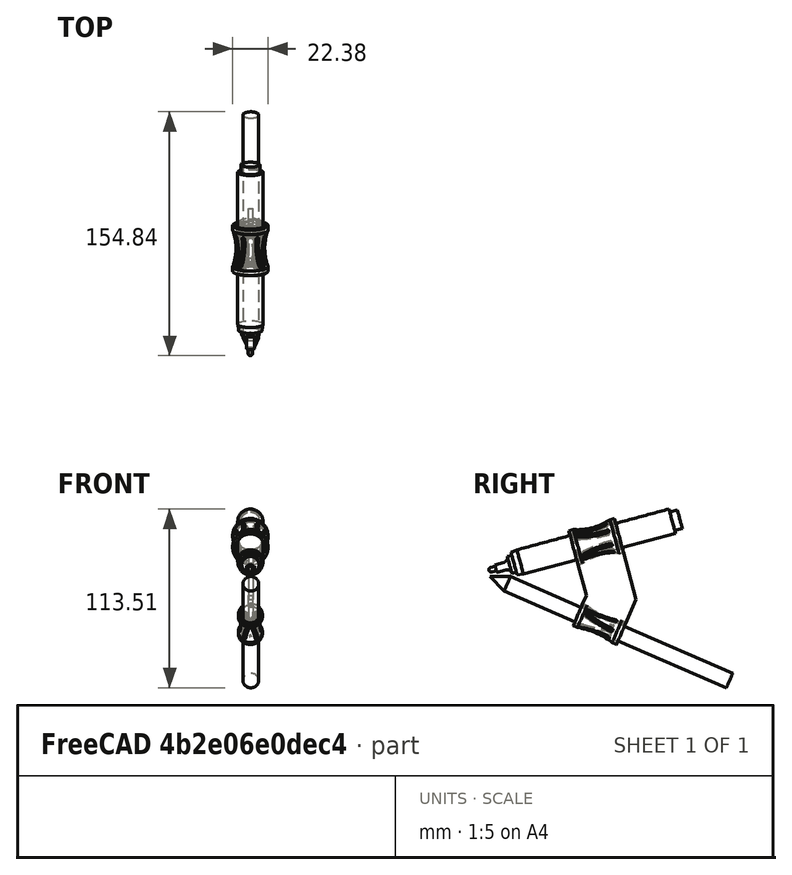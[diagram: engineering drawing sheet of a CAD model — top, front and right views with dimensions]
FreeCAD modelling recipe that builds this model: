
FCSTD DOCUMENT  (FreeCAD 1.0R39285 (Git))
Label: marker_holder_02
License: All rights reserved
LicenseURL: http://www.ohwr.org/attachments/2388/cern_ohl_v_1_2.txt
objects: PartDesign::SubShapeBinder×8, Sketcher::SketchObject×7, PartDesign::Plane×7, PartDesign::Body×5, PartDesign::Revolution×4, PartDesign::Line×3, PartDesign::Pocket×2, PartDesign::PolarPattern×2, PartDesign::Point×2, Mesh::Feature×1, PartDesign::Pad×1
note: 64 computed .brp shape members not serialized (recipe doc carries the construction recipe); baked Part::Feature solids carry a one-line shape summary decoded from their .brp

FEATURE [Mesh::Feature] Pencil_Hand_Pack
  Placement = pos=(0,0,0) rot=(-0.762035,0.457877,-0.457877;1.83927rad)
FEATURE [Sketcher::SketchObject] Sketch
  ArcFitTolerance = 1e-06
  AttachmentSupport = -> [YZ_Plane001]
  FullyConstrained = true
  MakeInternals = false
  MapMode = 5
  Placement = pos=(0,0,0) rot=(0.57735,0.57735,0.57735;2.0944rad)
  sketch-geometry (14):
    g0: LineSegment StartX=125.5 StartY=2e-16 StartZ=0 EndX=125.5 EndY=6 EndZ=0
    g1: LineSegment StartX=125.5 StartY=6 StartZ=0 EndX=120.5 EndY=6 EndZ=0
    g2: LineSegment StartX=120.5 StartY=6 StartZ=0 EndX=120.5 EndY=8 EndZ=0
    g3: LineSegment StartX=120.5 StartY=8 StartZ=0 EndX=28.5 EndY=8 EndZ=0
    g4: LineSegment StartX=28.5 StartY=8 StartZ=0 EndX=20.5 EndY=8 EndZ=0
    g5: LineSegment StartX=20.5 StartY=8 StartZ=0 EndX=16.5 EndY=7.5 EndZ=0
    g6: LineSegment StartX=16.5 StartY=7.5 StartZ=0 EndX=16.5 EndY=5.5 EndZ=0
    g7: LineSegment StartX=16.5 StartY=5.5 StartZ=0 EndX=13.5 EndY=5.5 EndZ=0
    g8: ArcOfCircle CenterX=10.5 CenterY=5.5 CenterZ=0 NormalX=0 NormalY=0 NormalZ=1 AngleXU=0 Radius=3 StartAngle=4.71239 EndAngle=6.28319
    g9: LineSegment StartX=10.5 StartY=2.5 StartZ=0 EndX=4.5 EndY=2.5 EndZ=0
    g10: LineSegment StartX=4.5 StartY=2.5 StartZ=0 EndX=4.5 EndY=1.5 EndZ=0
    g11: LineSegment StartX=4.5 StartY=1.5 StartZ=0 EndX=1.5 EndY=1.5 EndZ=0
    g12: ArcOfCircle CenterX=1.5 CenterY=0 CenterZ=0 NormalX=0 NormalY=0 NormalZ=1 AngleXU=0 Radius=1.5 StartAngle=1.5708 EndAngle=3.14159
    g13: LineSegment StartX=0 StartY=2e-16 StartZ=0 EndX=125.5 EndY=2e-16 EndZ=0
  constraints (40):
    c: Vertical(g0)
    c: Coincident(g0,g1)
    c: Horizontal(g1)
    c: Coincident(g1,g2)
    c: Vertical(g2)
    c: Coincident(g2,g3)
    c: Horizontal(g3)
    c: Coincident(g3,g4)
    c: Horizontal(g4)
    c: Coincident(g4,g5)
    c: Coincident(g5,g6)
    c: Vertical(g6)
    c: Coincident(g6,g7)
    c: Horizontal(g7)
    c: Perpendicular(g7,g8) = 4.71239
    c: Horizontal(g9)
    c: Coincident(g9,g10)
    c: Coincident(g10,g11)
    c: Horizontal(g11)
    c: Tangent(g11,g12) = -1.5708
    c: Perpendicular(g12,g-1)
    c: Radius(g12) = 1.5
    c: DistanceX(g11,g11) = 3
    c: Vertical(g10)
    c: Distance(g10,g10) = 1
    c: DistanceX(g9,g9) = 6
    c: Tangent(g8,g9) = 1.5708
    c: Radius(g8) = 3
    c: DistanceX(g7,g7) = 3
    c: DistanceX(g5,g4) = 4
    c: DistanceX(g4,g4) = 8
    c: DistanceX(g3,g3) = 92
    c: DistanceX(g1,g1) = 5
    c: DistanceY(g0,g0) = 6
    c: Distance(g2,g-1) = 8
    c: Coincident(g12,g-1)
    c: DistanceY(g5,g4) = 0.5
    c: Coincident(g13,g12)
    c: Coincident(g13,g0)
    c: Horizontal(g13)
FEATURE [PartDesign::Revolution] Revolution
  Angle = 360
  Angle2 = 60
  Axis = (0,1,0)
  Base = (0,0,0)
  Placement = pos=(0,0,0) rot=(1,1,1;2.0944rad)
  Profile = -> Sketch
  ReferenceAxis = -> Sketch [H_Axis]
  Refine = true
  Suppressed = false
  Type = 0
FEATURE [PartDesign::Body] Body001  label="Marker"
  AllowCompound = false
  Group = -> [Sketch,Revolution]
  Origin = -> Origin001
  Placement = pos=(74.7,-42.8,49.3) rot=(1,0,0;0.261799rad)
  Tip = -> Revolution
FEATURE [PartDesign::SubShapeBinder] Binder
  BindCopyOnChange = 0
  BindMode = 0
  ClaimChildren = false
  Context = -> Body [Binder.]
  Fuse = false
  MakeFace = true
  OffsetFill = false
  OffsetIntersection = false
  OffsetJoinType = 0
  OffsetOpenResult = false
  PartialLoad = false
  Refine = true
  Relative = true
  Support = -> [Body001]
  _Version = 2
FEATURE [PartDesign::Line] DatumLine
  AttacherType = Attacher::AttachEngineLine
  AttachmentSupport = -> [Binder]
  Length = 20
  MapMode = 19
  Placement = pos=(74.7,78.4237,81.7818) rot=(-0.519988,-0.519988,-0.677661;1.95044rad)
  ResizeMode = 0
FEATURE [PartDesign::Plane] DatumPlane
  AttachmentOffset = pos=(0,0,0) rot=(1,0,0;1.5708rad)
  AttachmentSupport = -> [DatumLine]
  Length = 131.506
  MapMode = 7
  Placement = pos=(74.7,78.4237,81.7818) rot=(1,0,0;3.40339rad)
  ResizeMode = 0
  Width = 193.795
FEATURE [PartDesign::Plane] DatumPlane001
  AttachmentSupport = -> [DatumLine]
  Length = 139.497
  MapMode = 3
  Placement = pos=(74.7,78.4237,81.7818) rot=(0.129428,-0.983106,-0.129428;1.58783rad)
  ResizeMode = 0
  Width = 194.678
FEATURE [PartDesign::Line] DatumLine001
  AttacherType = Attacher::AttachEngineLine
  AttachmentOffset = pos=(0,-104,0) rot=(1,0,0;0.671952rad)
  AttachmentSupport = -> [DatumLine]
  Length = 20
  MapMode = 29
  Placement = pos=(74.7,105.341,-18.6745) rot=(0,0.836286,0.548293;3.14159rad)
  ResizeMode = 0
FEATURE [Sketcher::SketchObject] Sketch001
  ArcFitTolerance = 1e-06
  AttachmentOffset = pos=(0,0,75) rot=(0,0,1;0rad)
  AttachmentSupport = -> [YZ_Plane]
  ExternalGeometry = -> [DatumLine,DatumLine001]
  FullyConstrained = true
  MakeInternals = false
  MapMode = 5
  Placement = pos=(75,0,0) rot=(0.57735,0.57735,0.57735;2.0944rad)
  sketch-geometry (4):
    g0: LineSegment StartX=108.006 StartY=-25.2856 StartZ=0 EndX=-33.221 EndY=36.1217 EndZ=0
    g1: LineSegment StartX=-33.221 StartY=36.1217 StartZ=0 EndX=-42.232 EndY=45.492 EndZ=0
    g2: LineSegment StartX=-42.232 StartY=45.492 StartZ=0 EndX=110 EndY=-20.7003 EndZ=0
    g3: LineSegment StartX=108.006 StartY=-25.2856 StartZ=0 EndX=110 EndY=-20.7003 EndZ=0
  constraints (12):
    c: Coincident(g0,g1)
    c: Coincident(g1,g2)
    c: PointOnObject(g1,g-4)
    c: Distance(g2,g0) = 5
    c: Coincident(g3,g0)
    c: Coincident(g3,g2)
    c: PointOnObject(g2,g-4)
    c: Perpendicular(g2,g3)
    c: Perpendicular(g0,g3)
    c: DistanceX(g2) = 110
    c: Distance(g2,g2) = 166
    c: Distance(g0,g0) = 154
FEATURE [PartDesign::Revolution] Revolution001
  Angle = 360
  Angle2 = 60
  Axis = (0,0.91706,-0.398749)
  Base = (75,-42.232,45.492)
  Placement = pos=(0,0,0) rot=(1,1,1;2.0944rad)
  Profile = -> Sketch001
  ReferenceAxis = -> Sketch001 [Edge3]
  Refine = true
  Reversed = true
  Suppressed = false
  Type = 0
FEATURE [PartDesign::Body] Body  label="Pencil"
  AllowCompound = false
  Group = -> [Binder,DatumLine,DatumPlane,DatumPlane001,DatumLine001,Sketch001,Revolution001]
  Origin = -> Origin
  Tip = -> Revolution001
FEATURE [PartDesign::SubShapeBinder] Binder001
  BindCopyOnChange = 0
  BindMode = 0
  ClaimChildren = false
  Context = -> Body002 [Binder001.]
  Fuse = false
  MakeFace = true
  OffsetFill = false
  OffsetIntersection = false
  OffsetJoinType = 0
  OffsetOpenResult = false
  PartialLoad = false
  Refine = true
  Relative = true
  Support = -> [Body]
  _Version = 2
FEATURE [PartDesign::SubShapeBinder] Binder002
  BindCopyOnChange = 0
  BindMode = 0
  ClaimChildren = false
  Context = -> Body002 [Binder002.]
  Fuse = false
  MakeFace = true
  OffsetFill = false
  OffsetIntersection = false
  OffsetJoinType = 0
  OffsetOpenResult = false
  PartialLoad = false
  Refine = true
  Relative = true
  Support = -> [Body001]
  _Version = 2
FEATURE [PartDesign::Plane] DatumPlane002
  AttachmentOffset = pos=(0,0,-78) rot=(0,0,1;0rad)
  AttachmentSupport = -> [Binder001]
  Length = 134.38
  MapMode = 5
  Placement = pos=(1.42e-14,28.5489,-12.4134) rot=(0,0.836286,0.548293;3.14159rad)
  ResizeMode = 0
  Width = 158.106
FEATURE [PartDesign::Plane] DatumPlane003
  AttachmentOffset = pos=(0,0,-40) rot=(0,0,1;0rad)
  AttachmentSupport = -> [Binder002]
  Length = 132.368
  MapMode = 5
  Placement = pos=(0,54.9787,14.7315) rot=(0,0.608761,0.793353;3.14159rad)
  ResizeMode = 0
  Width = 134.827
FEATURE [PartDesign::Plane] DatumPlane005
  AttachmentOffset = pos=(0,0,0) rot=(0.250563,0.935113,-0.250563;1.63783rad)
  AttachmentSupport = -> [Binder001]
  Length = 225.193
  MapMode = 7
  Placement = pos=(75,108.006,-25.2856) rot=(-0.597976,0.761197,0.251005;4.1221rad)
  ResizeMode = 0
  Width = 206.922
FEATURE [Sketcher::SketchObject] Sketch002
  ArcFitTolerance = 1e-06
  AttachmentSupport = -> [DatumPlane005]
  ExternalGeometry = -> [Binder001]
  FullyConstrained = true
  MakeInternals = false
  MapMode = 5
  Placement = pos=(75,108.006,-25.2856) rot=(-0.597976,0.761197,0.251005;4.1221rad)
  sketch-geometry (11):
    g0: LineSegment [constr] StartX=166 StartY=4.33013 StartZ=0 EndX=8.53e-14 EndY=4.33013 EndZ=0
    g1: LineSegment StartX=105 StartY=-0.8 StartZ=0 EndX=105 EndY=-2.8 EndZ=0
    g2: LineSegment StartX=105 StartY=-2.8 StartZ=0 EndX=102 EndY=-2.8 EndZ=0
    g3: ArcOfCircle CenterX=90 CenterY=-93.95 CenterZ=0 NormalX=0 NormalY=0 NormalZ=1 AngleXU=0 Radius=94.35 StartAngle=1.41114 EndAngle=1.73046
    g4: LineSegment StartX=75 StartY=-0.8 StartZ=0 EndX=75 EndY=-2.8 EndZ=0
    g5: LineSegment [constr] StartX=75 StartY=-0.8 StartZ=0 EndX=105 EndY=-0.8 EndZ=0
    g6: LineSegment [constr] StartX=90 StartY=-93.95 StartZ=0 EndX=90 EndY=-2.8 EndZ=0
    g7: LineSegment [constr] StartX=90 StartY=-2.8 StartZ=0 EndX=90 EndY=-0.8 EndZ=0
    g8: LineSegment [constr] StartX=90 StartY=-0.8 StartZ=0 EndX=90 EndY=0.4 EndZ=0
    g9: ArcOfCircle CenterX=90 CenterY=-47 CenterZ=0 NormalX=0 NormalY=0 NormalZ=1 AngleXU=0 Radius=45.8 StartAngle=1.30569 EndAngle=1.8359
    g10: LineSegment StartX=78 StartY=-2.8 StartZ=0 EndX=75 EndY=-2.8 EndZ=0
  constraints (32):
    c: Coincident(g0,g-5)
    c: Symmetric(g-6,g-6,g0)
    c: Coincident(g1,g2)
    c: Horizontal(g2)
    c: Coincident(g3,g1)
    c: Coincident(g4,g3)
    c: Coincident(g4,g10)
    c: Vertical(g4)
    c: Vertical(g1)
    c: Equal(g1,g4)
    c: DistanceX(g10,g2) = 30
    c: DistanceY(g4,g4) = 2
    c: Coincident(g5,g3)
    c: Coincident(g5,g1)
    c: Coincident(g6,g3)
    c: Symmetric(g2,g10,g6)
    c: Coincident(g7,g6)
    c: Symmetric(g5,g5,g7)
    c: Coincident(g8,g7)
    c: PointOnObject(g8,g3)
    c: Vertical(g8)
    c: Distance(g3,g-3) = 0.8
    c: Distance(g8,g8) = 1.2
    c: PointOnObject(g9,g6)
    c: PointOnObject(g9,g10)
    c: PointOnObject(g10,g9)
    c: Coincident(g2,g9)
    c: Equal(g10,g2)
    c: Distance(g10,g10) = 3
    c: Horizontal(g10)
    c: Distance(g8,g9) = 1.6
    c: DistanceX(g-1,g3) = 90
FEATURE [PartDesign::SubShapeBinder] Binder003
  BindCopyOnChange = 0
  BindMode = 0
  ClaimChildren = false
  Context = -> Body002 [Binder003.]
  Fuse = false
  MakeFace = true
  OffsetFill = false
  OffsetIntersection = false
  OffsetJoinType = 0
  OffsetOpenResult = false
  PartialLoad = false
  Refine = true
  Relative = true
  Support = -> [Body[DatumLine001.]]
  _Version = 2
FEATURE [PartDesign::Revolution] Revolution002
  Angle = 360
  Angle2 = 60
  Axis = (0,0.91706,-0.398749)
  Base = (74.7,105.341,-18.6745)
  Placement = pos=(75,108.006,-25.2856) rot=(-0.597976,0.761197,0.251005;4.1221rad)
  Profile = -> Sketch002
  ReferenceAxis = -> Binder003 [Edge1]
  Refine = true
  Reversed = true
  Suppressed = false
  Type = 0
FEATURE [Sketcher::SketchObject] Sketch003
  ArcFitTolerance = 1e-06
  AttachmentSupport = -> [DatumPlane005]
  ExternalGeometry = -> [Binder003,Revolution002]
  FullyConstrained = true
  MakeInternals = false
  MapMode = 5
  Placement = pos=(75,108.006,-25.2856) rot=(-0.597976,0.761197,0.251005;4.1221rad)
  sketch-geometry (15):
    g0: ArcOfCircle CenterX=99 CenterY=4.48013 CenterZ=0 NormalX=0 NormalY=0 NormalZ=1 AngleXU=0 Radius=0.8 StartAngle=4.83492 EndAngle=7.73145
    g1: ArcOfCircle [constr] CenterX=81 CenterY=4.48013 CenterZ=0 NormalX=0 NormalY=0 NormalZ=1 AngleXU=0 Radius=3 StartAngle=1.44827 EndAngle=4.83492
    g2: LineSegment StartX=99.0978 StartY=3.68612 StartZ=0 EndX=81.3667 EndY=1.50262 EndZ=0
    g3: LineSegment StartX=99.0978 StartY=5.27413 StartZ=0 EndX=81.3667 EndY=7.45764 EndZ=0
    g4: ArcOfCircle CenterX=81.4644 CenterY=0.708617 CenterZ=0 NormalX=0 NormalY=0 NormalZ=1 AngleXU=0 Radius=0.8 StartAngle=1.69332 EndAngle=4.83492
    g5: ArcOfCircle CenterX=81.4644 CenterY=8.25164 CenterZ=0 NormalX=0 NormalY=0 NormalZ=1 AngleXU=0 Radius=0.8 StartAngle=1.44827 EndAngle=4.58986
    g6: LineSegment [constr] StartX=81 StartY=4.48013 StartZ=0 EndX=81.3667 EndY=1.50262 EndZ=0
    g7: LineSegment [constr] StartX=81.3667 StartY=1.50262 StartZ=0 EndX=81.4644 EndY=0.708617 EndZ=0
    g8: ArcOfCircle CenterX=99 CenterY=4.48013 CenterZ=0 NormalX=0 NormalY=0 NormalZ=1 AngleXU=0 Radius=2.4 StartAngle=4.83492 EndAngle=7.73145
    g9: LineSegment StartX=99.2933 StartY=2.09812 StartZ=0 EndX=81.5622 EndY=-0.0853857 EndZ=0
    g10: LineSegment StartX=81.5622 StartY=9.04564 StartZ=0 EndX=99.2933 EndY=6.86213 EndZ=0
    g11: LineSegment [constr] StartX=81 StartY=4.48013 StartZ=0 EndX=81.3667 EndY=7.45764 EndZ=0
    g12: LineSegment [constr] StartX=81.3667 StartY=7.45764 StartZ=0 EndX=81.4644 EndY=8.25164 EndZ=0
    g13: LineSegment [constr] StartX=78 StartY=4.48013 StartZ=0 EndX=81 EndY=4.48013 EndZ=0
    g14: LineSegment [constr] StartX=102 StartY=4.48013 StartZ=0 EndX=99 EndY=4.48013 EndZ=0
  constraints (34):
    c: Tangent(g0,g2) = 1.5708
    c: Tangent(g0,g3) = -1.5708
    c: Tangent(g1,g2) = 1.5708
    c: Tangent(g1,g3) = -1.5708
    c: Radius(g0) = 0.8
    c: Radius(g1) = 3
    c: Equal(g4,g0)
    c: Coincident(g6,g1)
    c: Coincident(g7,g1)
    c: Coincident(g7,g4)
    c: Tangent(g5,g10) = 1.5708
    c: Tangent(g4,g9) = 1.5708
    c: Coincident(g4,g2)
    c: Tangent(g8,g10) = 1.5708
    c: Tangent(g5,g3) = 1.5708
    c: Parallel(g9,g2)
    c: Tangent(g8,g9) = 1.5708
    c: Equal(g4,g5)
    c: Coincident(g11,g1)
    c: Coincident(g12,g11)
    c: Coincident(g12,g5)
    c: Parallel(g11,g12)
    c: Parallel(g7,g6)
    c: Coincident(g6,g1)
    c: Equal(g6,g11)
    c: Coincident(g8,g0)
    c: PointOnObject(g11,g-3)
    c: PointOnObject(g0,g-3)
    c: Symmetric(g-4,g-4,g13)
    c: Coincident(g13,g11)
    c: Symmetric(g-5,g-5,g14)
    c: Coincident(g14,g0)
    c: Equal(g14,g13)
    c: DistanceX(g13,g13) = 3
FEATURE [PartDesign::Pocket] Pocket
  BaseFeature = -> Revolution002
  Direction = (0.866025,0.199375,0.45853)
  Length = 5
  Length2 = 5
  Placement = pos=(75,108.006,-25.2856) rot=(-0.597976,0.761197,0.251005;4.1221rad)
  Profile = -> Sketch003
  ReferenceAxis = -> Sketch003 [N_Axis]
  Refine = true
  Suppressed = false
  Type = 1
FEATURE [PartDesign::PolarPattern] PolarPattern
  Angle = 360
  Axis = -> Binder003 [Edge1]
  BaseFeature = -> Pocket
  Mode = 0
  Occurrences = 3
  Offset = 120
  Originals = -> [Pocket]
  Placement = pos=(75,108.006,-25.2856) rot=(-0.597976,0.761197,0.251005;4.1221rad)
  Refine = true
  Suppressed = false
  TransformMode = 0
FEATURE [PartDesign::Body] Body002  label="Pencil_holder"
  AllowCompound = false
  Group = -> [Binder001,Binder002,DatumPlane002,DatumPlane003,DatumPlane005,Sketch002,Binder003,Revolution002,Sketch003,Pocket,PolarPattern]
  Origin = -> Origin002
  Tip = -> PolarPattern
FEATURE [PartDesign::SubShapeBinder] Binder004
  BindCopyOnChange = 0
  BindMode = 0
  ClaimChildren = false
  Context = -> Body003 [Binder004.]
  Fuse = false
  MakeFace = true
  OffsetFill = false
  OffsetIntersection = false
  OffsetJoinType = 0
  OffsetOpenResult = false
  PartialLoad = false
  Refine = true
  Relative = true
  Support = -> [Body001]
  _Version = 2
FEATURE [PartDesign::SubShapeBinder] Binder005
  BindCopyOnChange = 0
  BindMode = 0
  ClaimChildren = false
  Context = -> Body003 [Binder005.]
  Fuse = false
  MakeFace = true
  OffsetFill = false
  OffsetIntersection = false
  OffsetJoinType = 0
  OffsetOpenResult = false
  PartialLoad = false
  Refine = true
  Relative = true
  Support = -> [Body002]
  _Version = 2
FEATURE [PartDesign::Plane] DatumPlane006
  AttachmentOffset = pos=(0,0,0) rot=(0.357407,0.862856,-0.357407;1.71777rad)
  AttachmentSupport = -> [Binder004]
  Length = 151.965
  MapMode = 8
  Placement = pos=(74.7,71.5235,88.2151) rot=(-0.694747,0.622893,0.359627;3.50969rad)
  ResizeMode = 0
  Width = 206.11
FEATURE [PartDesign::Point] DatumPoint
  AttacherType = Attacher::AttachEnginePoint
  AttachmentSupport = -> [Binder004]
  MapMode = 37
  Placement = pos=(74.7,-42.8,49.3) rot=(0,0,1;0rad)
FEATURE [PartDesign::Point] DatumPoint001
  AttacherType = Attacher::AttachEnginePoint
  AttachmentSupport = -> [Binder004]
  MapMode = 37
  Placement = pos=(74.7,78.4237,81.7818) rot=(0,0,1;0rad)
FEATURE [PartDesign::Line] DatumLine002
  AttacherType = Attacher::AttachEngineLine
  AttachmentSupport = -> [DatumPoint,DatumPoint001]
  Length = 20
  MapMode = 29
  Placement = pos=(74.7,-42.8,49.3) rot=(0,0.608761,0.793353;3.14159rad)
  ResizeMode = 0
FEATURE [Sketcher::SketchObject] Sketch005
  ArcFitTolerance = 1e-06
  AttachmentSupport = -> [DatumPlane006]
  ExternalGeometry = -> [Binder004]
  FullyConstrained = true
  MakeInternals = false
  MapMode = 5
  Placement = pos=(74.7,71.5235,88.2151) rot=(0.694747,-0.622893,-0.359627;2.77349rad)
  sketch-geometry (12):
    g0: LineSegment StartX=35 StartY=4 StartZ=0 EndX=35 EndY=1.5 EndZ=0
    g1: LineSegment StartX=35 StartY=1.5 StartZ=0 EndX=37 EndY=1.5 EndZ=0
    g2: LineSegment StartX=65 StartY=1.5 StartZ=0 EndX=65 EndY=4 EndZ=0
    g3: LineSegment StartX=65 StartY=4 StartZ=0 EndX=62 EndY=4 EndZ=0
    g4: ArcOfCircle CenterX=50 CenterY=31.55 CenterZ=0 NormalX=0 NormalY=0 NormalZ=1 AngleXU=0 Radius=30.05 StartAngle=4.3016 EndAngle=5.12318
    g5: ArcOfCircle CenterX=50 CenterY=32.7 CenterZ=0 NormalX=0 NormalY=0 NormalZ=1 AngleXU=0 Radius=33.8 StartAngle=4.3176 EndAngle=5.10718
    g6: LineSegment StartX=38 StartY=4 StartZ=0 EndX=35 EndY=4 EndZ=0
    g7: LineSegment StartX=63 StartY=1.5 StartZ=0 EndX=65 EndY=1.5 EndZ=0
    g8: LineSegment [constr] StartX=37 StartY=1.5 StartZ=0 EndX=63 EndY=1.5 EndZ=0
    g9: LineSegment [constr] StartX=50 StartY=-1.1 StartZ=0 EndX=50 EndY=1.5 EndZ=0
    g10: LineSegment [constr] StartX=50 StartY=1.5 StartZ=0 EndX=50 EndY=32.7 EndZ=0
    g11: LineSegment [constr] StartX=50 StartY=32.7 StartZ=0 EndX=50 EndY=31.55 EndZ=0
  constraints (37):
    c: Coincident(g0,g1)
    c: Coincident(g7,g2)
    c: Coincident(g2,g3)
    c: Coincident(g6,g0)
    c: Vertical(g0)
    c: Vertical(g2)
    c: Horizontal(g1)
    c: Horizontal(g3)
    c: PointOnObject(g4,g6)
    c: PointOnObject(g5,g7)
    c: Coincident(g3,g4)
    c: PointOnObject(g6,g4)
    c: Coincident(g1,g5)
    c: PointOnObject(g7,g5)
    c: Equal(g6,g3)
    c: Equal(g1,g7)
    c: Equal(g0,g2)
    c: Horizontal(g7)
    c: Horizontal(g6)
    c: Horizontal(g4,g3)
    c: DistanceY(g2,g2) = 2.5
    c: DistanceX(g3,g3) = 3
    c: Distance(g7,g7) = 2
    c: Coincident(g8,g1)
    c: Coincident(g8,g5)
    c: PointOnObject(g9,g5)
    c: Symmetric(g8,g8,g9)
    c: Vertical(g9)
    c: Coincident(g10,g9)
    c: Coincident(g10,g5)
    c: Coincident(g11,g5)
    c: Coincident(g11,g4)
    c: DistanceY(g9,g9) = 2.6
    c: DistanceX(g0,g2) = 30
    c: DistanceY(g-1,g0) = 1.5
    c: Distance(g5,g-2) = 50
    c: Tangent(g4,g8)
FEATURE [PartDesign::Revolution] Revolution003
  Angle = 360
  Angle2 = 60
  Axis = (0,0.965926,0.258819)
  Base = (74.7,-42.8,49.3)
  Placement = pos=(74.7,71.5235,88.2151) rot=(-0.694747,0.622893,0.359627;3.50969rad)
  Profile = -> Sketch005
  ReferenceAxis = -> DatumLine002
  Refine = true
  Reversed = true
  Suppressed = false
  Type = 0
FEATURE [Sketcher::SketchObject] Sketch006
  ArcFitTolerance = 1e-06
  AttachmentSupport = -> [DatumPlane006]
  ExternalGeometry = -> [Revolution003]
  FullyConstrained = true
  MakeInternals = false
  MapMode = 5
  Placement = pos=(74.7,71.5235,88.2151) rot=(0.694747,-0.622893,-0.359627;2.77349rad)
  sketch-geometry (16):
    g0: ArcOfCircle [constr] CenterX=41 CenterY=-5.65685 CenterZ=0 NormalX=0 NormalY=0 NormalZ=1 AngleXU=0 Radius=2.5 StartAngle=1.47621 EndAngle=4.80697
    g1: ArcOfCircle CenterX=59 CenterY=-5.65685 CenterZ=0 NormalX=0 NormalY=0 NormalZ=1 AngleXU=0 Radius=0.8 StartAngle=4.80697 EndAngle=7.7594
    g2: LineSegment StartX=41.2361 StartY=-3.16803 StartZ=0 EndX=59.0756 EndY=-4.86043 EndZ=0
    g3: LineSegment StartX=41.2361 StartY=-8.14568 StartZ=0 EndX=59.0756 EndY=-6.45328 EndZ=0
    g4: LineSegment [constr] StartX=37 StartY=-5.65685 StartZ=0 EndX=41 EndY=-5.65685 EndZ=0
    g5: LineSegment [constr] StartX=41 StartY=-5.65685 StartZ=0 EndX=59 EndY=-5.65685 EndZ=0
    g6: LineSegment [constr] StartX=59 StartY=-5.65685 StartZ=0 EndX=63 EndY=-5.65685 EndZ=0
    g7: ArcOfCircle CenterX=41.3117 CenterY=-8.9421 CenterZ=0 NormalX=0 NormalY=0 NormalZ=1 AngleXU=0 Radius=0.8 StartAngle=1.66538 EndAngle=4.80697
    g8: ArcOfCircle CenterX=41.3117 CenterY=-2.3716 CenterZ=0 NormalX=0 NormalY=0 NormalZ=1 AngleXU=0 Radius=0.8 StartAngle=1.47621 EndAngle=4.6178
    g9: ArcOfCircle CenterX=59 CenterY=-5.65685 CenterZ=0 NormalX=0 NormalY=0 NormalZ=1 AngleXU=0 Radius=2.4 StartAngle=4.80697 EndAngle=7.7594
    g10: LineSegment [constr] StartX=41 StartY=-5.65685 StartZ=0 EndX=41.2361 EndY=-8.14568 EndZ=0
    g11: LineSegment [constr] StartX=41.2361 StartY=-8.14568 StartZ=0 EndX=41.3117 EndY=-8.9421 EndZ=0
    g12: LineSegment [constr] StartX=41 StartY=-5.65685 StartZ=0 EndX=41.2361 EndY=-3.16803 EndZ=0
    g13: LineSegment [constr] StartX=41.2361 StartY=-3.16803 StartZ=0 EndX=41.3117 EndY=-2.3716 EndZ=0
    g14: LineSegment StartX=41.3872 StartY=-9.73853 StartZ=0 EndX=59.2267 EndY=-8.04613 EndZ=0
    g15: LineSegment StartX=59.2267 StartY=-3.26758 StartZ=0 EndX=41.3872 EndY=-1.57518 EndZ=0
  constraints (35):
    c: Tangent(g0,g2) = 1.5708
    c: Tangent(g1,g2) = 1.5708
    c: Symmetric(g-4,g-4,g4)
    c: Symmetric(g-3,g-3,g6)
    c: Equal(g4,g6)
    c: Coincident(g12,g0)
    c: Coincident(g13,g0)
    c: Coincident(g13,g8)
    c: Radius(g1) = 0.8
    c: Radius(g0) = 2.5
    c: Equal(g8,g1)
    c: Coincident(g10,g3)
    c: Coincident(g7,g11)
    c: Parallel(g11,g10)
    c: Tangent(g0,g3) = -1.5708
    c: Coincident(g11,g0)
    c: Parallel(g5,g6)
    c: Tangent(g1,g3) = -1.5708
    c: Parallel(g4,g5)
    c: Parallel(g2,g15)
    c: Tangent(g9,g15) = -1.5708
    c: Tangent(g9,g14) = -1.5708
    c: Tangent(g7,g14) = -1.5708
    c: Coincident(g7,g0)
    c: Tangent(g8,g2) = -1.5708
    c: Tangent(g8,g15) = -1.5708
    c: Equal(g1,g7)
    c: DistanceX(g4,g4) = 4
    c: Coincident(g4,g5)
    c: Coincident(g9,g1)
    c: Coincident(g0,g10)
    c: Coincident(g0,g12)
    c: Coincident(g5,g6)
    c: Coincident(g0,g4)
    c: Coincident(g5,g1)
FEATURE [PartDesign::Pocket] Pocket001
  BaseFeature = -> Revolution003
  Direction = (0.707107,-0.183013,0.683013)
  Length = 5
  Length2 = 5
  Placement = pos=(74.7,71.5235,88.2151) rot=(-0.694747,0.622893,0.359627;3.50969rad)
  Profile = -> Sketch006
  ReferenceAxis = -> Sketch006 [N_Axis]
  Refine = true
  Suppressed = false
  Type = 1
FEATURE [PartDesign::PolarPattern] PolarPattern001
  Angle = 360
  Axis = -> DatumLine002
  BaseFeature = -> Pocket001
  Mode = 0
  Occurrences = 4
  Offset = 120
  Originals = -> [Pocket001]
  Placement = pos=(74.7,71.5235,88.2151) rot=(-0.694747,0.622893,0.359627;3.50969rad)
  Refine = true
  Suppressed = false
  TransformMode = 0
FEATURE [PartDesign::Body] Body003  label="Marker_holder"
  AllowCompound = false
  Group = -> [Binder004,Binder005,DatumPlane006,DatumPoint,DatumPoint001,DatumLine002,Sketch005,Revolution003,Sketch006,Pocket001,PolarPattern001]
  Origin = -> Origin003
  Tip = -> PolarPattern001
FEATURE [PartDesign::SubShapeBinder] Binder006
  BindCopyOnChange = 0
  BindMode = 0
  ClaimChildren = false
  Context = -> Body004 [Binder006.]
  Fuse = false
  MakeFace = true
  OffsetFill = false
  OffsetIntersection = false
  OffsetJoinType = 0
  OffsetOpenResult = false
  PartialLoad = false
  Refine = true
  Relative = true
  Support = -> [Body002]
  _Version = 2
FEATURE [PartDesign::SubShapeBinder] Binder007
  BindCopyOnChange = 0
  BindMode = 0
  ClaimChildren = false
  Context = -> Body004 [Binder007.]
  Fuse = false
  MakeFace = true
  OffsetFill = false
  OffsetIntersection = false
  OffsetJoinType = 0
  OffsetOpenResult = false
  PartialLoad = false
  Refine = true
  Relative = true
  Support = -> [Body003]
  _Version = 2
FEATURE [PartDesign::Plane] DatumPlane007
  AttachmentOffset = pos=(3,0,0) rot=(0,1,0;1.5708rad)
  AttachmentSupport = -> [Binder007]
  Length = 126.457
  MapMode = 7
  Placement = pos=(74.8716,34.0863,81.112) rot=(0.621515,0.476905,0.621515;2.25159rad)
  ResizeMode = 0
  Width = 145.567
FEATURE [Sketcher::SketchObject] Sketch007
  ArcFitTolerance = 1e-06
  AttachmentSupport = -> [DatumPlane007]
  ExternalGeometry = -> [Binder006]
  FullyConstrained = true
  MakeInternals = false
  MapMode = 5
  Placement = pos=(74.8716,34.0863,81.112) rot=(0.621515,0.476905,0.621515;2.25159rad)
  sketch-geometry (13):
    g0: LineSegment StartX=3 StartY=-21.75 StartZ=0 EndX=3 EndY=-52.7975 EndZ=0
    g1: LineSegment StartX=-7.56344 StartY=-66.0776 StartZ=0 EndX=-9.91127 EndY=-64.21 EndZ=0
    g2: LineSegment StartX=-24 StartY=-21.75 StartZ=0 EndX=-27 EndY=-21.75 EndZ=0
    g3: LineSegment [constr] StartX=-27 StartY=-21.75 StartZ=0 EndX=-31.0417 EndY=-47.4021 EndZ=0
    g4: LineSegment StartX=-31.0417 StartY=-47.4021 StartZ=0 EndX=-28.6939 EndY=-49.2697 EndZ=0
    g5: ArcOfCircle CenterX=-12 CenterY=-49.3 CenterZ=0 NormalX=0 NormalY=0 NormalZ=1 AngleXU=0 Radius=30.05 StartAngle=1.16001 EndAngle=1.98159
    g6: LineSegment StartX=-2.66e-14 StartY=-21.75 StartZ=0 EndX=3 EndY=-21.75 EndZ=0
    g7: ArcOfCircle CenterX=8.21258 CenterY=-22.1486 CenterZ=0 NormalX=0 NormalY=0 NormalZ=1 AngleXU=0 Radius=45.8 StartAngle=3.77533 EndAngle=4.30554
    g8: LineSegment [constr] StartX=-28.6939 StartY=-49.2697 StartZ=0 EndX=-9.91127 EndY=-64.21 EndZ=0
    g9: LineSegment [constr] StartX=-20.2986 StartY=-57.992 StartZ=0 EndX=-19.3026 EndY=-56.7398 EndZ=0
    g10: LineSegment StartX=-7.56344 StartY=-66.0776 StartZ=0 EndX=3 EndY=-52.7975 EndZ=0
    g11: LineSegment StartX=-27 StartY=-21.75 StartZ=0 EndX=-27 EndY=-42.321 EndZ=0
    g12: LineSegment StartX=-31.0417 StartY=-47.4021 StartZ=0 EndX=-27 EndY=-42.321 EndZ=0
  constraints (35):
    c: Vertical(g0)
    c: Equal(g5,g-7)
    c: PointOnObject(g9,g7)
    c: Symmetric(g8,g8,g9)
    c: Perpendicular(g9,g8)
    c: Distance(g9,g9) = 1.6
    c: Coincident(g0,g10)
    c: PointOnObject(g4,g-10)
    c: Symmetric(g-16,g-5,g4)
    c: Coincident(g3,g4)
    c: Symmetric(g-6,g-15,g1)
    c: Perpendicular(g-6,g1)
    c: PointOnObject(g1,g-11)
    c: Coincident(g10,g1)
    c: Coincident(g7,g1)
    c: Coincident(g7,g4)
    c: Perpendicular(g4,g-5)
    c: Coincident(g8,g4)
    c: Coincident(g8,g1)
    c: Symmetric(g-3,g-12,g2)
    c: PointOnObject(g2,g-8)
    c: Perpendicular(g2,g-3)
    c: Coincident(g3,g2)
    c: Coincident(g5,g2)
    c: Symmetric(g-14,g-4,g6)
    c: PointOnObject(g6,g-9)
    c: Perpendicular(g6,g-4)
    c: Coincident(g0,g6)
    c: Coincident(g5,g6)
    c: Coincident(g11,g2)
    c: Vertical(g11)
    c: Coincident(g12,g3)
    c: Coincident(g11,g12)
    c: Parallel(g12,g10)
    c: Perpendicular(g10,g1)
FEATURE [PartDesign::Pad] Pad
  Direction = (1,1e-16,-1e-16)
  Length = 3
  Length2 = 10
  Midplane = true
  Placement = pos=(74.8716,34.0863,81.112) rot=(0.621515,0.476905,0.621515;2.25159rad)
  Profile = -> Sketch007
  ReferenceAxis = -> Sketch007 [N_Axis]
  Refine = true
  Suppressed = false
  Type = 0
FEATURE [PartDesign::Body] Body004  label="Bridge"
  AllowCompound = false
  Group = -> [Binder006,Binder007,DatumPlane007,Sketch007,Pad]
  Origin = -> Origin004
  Tip = -> Pad
